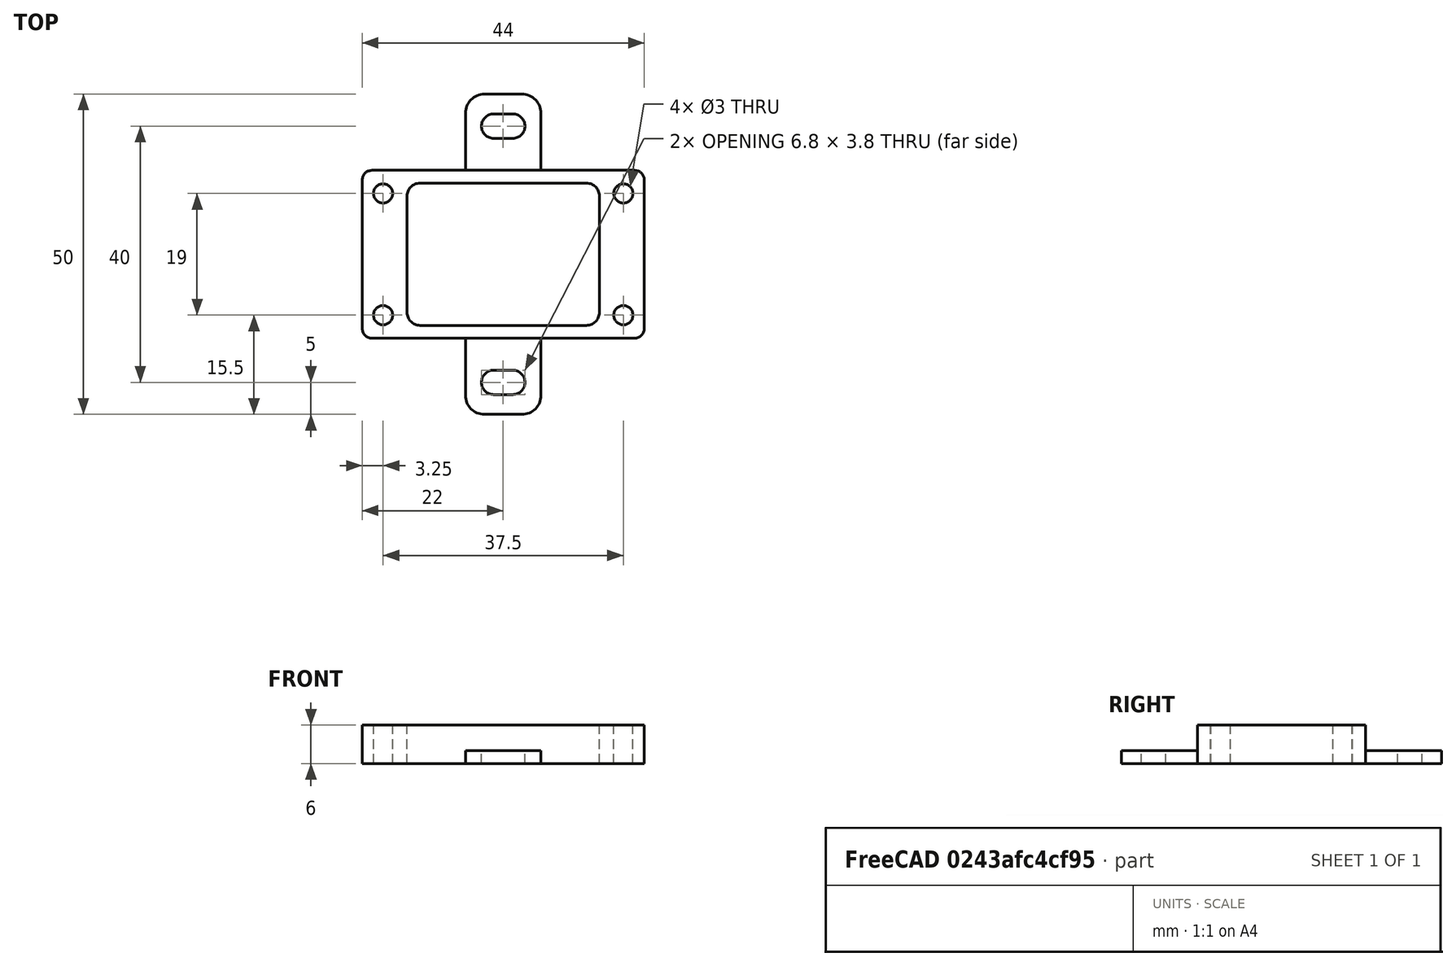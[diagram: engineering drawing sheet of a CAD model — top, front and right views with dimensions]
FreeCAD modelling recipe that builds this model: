
FCSTD DOCUMENT  (FreeCAD 0.19R23578 (Git))
Label: step_up_xl6019e1_en
License: All rights reserved
LicenseURL: http://en.wikipedia.org/wiki/All_rights_reserved
objects: Part::Box×2, Part::Fillet×2, Part::MultiFuse×2, Spreadsheet::Sheet×1, Part::Cylinder×1, Part::FeaturePython×1, Part::Feature×1, Part::Cut×1, App::Part×1
note: 10 computed .brp shape members not serialized (recipe doc carries the construction recipe); baked Part::Feature solids carry a one-line shape summary decoded from their .brp

FEATURE [Spreadsheet::Sheet] Spreadsheet  label="p"
  cells = A1=hole_x_dist; B1(hole_x_dist)=37.5; A2=hole_y_dist; B2(hole_y_dist)==pcb_y - 2 * 3.6; A3=pcb_under; B3(pcb_under)=6; A4=pcb_x; B4(pcb_x)=44; A5=pcb_y; B5(pcb_y)=26.2; A6=hole_r; B6(hole_r)=1.5; A7=under_pcb_border_x; B7(under_pcb_border_x)=7; A8=under_pcb_border_y; B8(under_pcb_border_y)=2
FEATURE [Part::Box] Box  label="bottom cube"
  AttacherType = Attacher::AttachEngine3D
  Height = 6
  Length = 44
  Width = 26.2
  expr: Width = <<p>>.pcb_y
  expr: Length = <<p>>.pcb_x
  expr: Height = <<p>>.pcb_under
FEATURE [Part::Box] Box001  label="bottom extraction cube"
  AttacherType = Attacher::AttachEngine3D
  Height = 10
  Length = 30
  Placement = pos=(7,2,0) rot=(0,0,1;0rad)
  Width = 22.2
  expr: .Placement.Base.y = Spreadsheet.under_pcb_border_y
  expr: .Placement.Base.x = Spreadsheet.under_pcb_border_x
  expr: Length = <<p>>.pcb_x - <<p>>.under_pcb_border_x * 2
  expr: Width = <<p>>.pcb_y - <<p>>.under_pcb_border_y * 2
FEATURE [Part::Cylinder] Cylinder  label="pcb hole"
  Angle = 360
  AttacherType = Attacher::AttachEngine3D
  Height = 10
  Radius = 1.5
  expr: Radius = <<p>>.hole_r
FEATURE [Part::FeaturePython] Array001  label="hole array"  # Draft array (typed FeaturePython)
  Angle = 360
  ArrayType = 0
  Axis = (0,0,1)
  Base = -> Cylinder
  Center = (0,0,0)
  Fuse = false
  IntervalAxis = (0,0,0)
  IntervalX = (37.5,0,0)
  IntervalY = (0,19,0)
  IntervalZ = (0,0,1)
  NumberPolar = 1
  NumberX = 2
  NumberY = 2
  NumberZ = 1
  Placement = pos=(3.25,3.6,0) rot=(0,0,1;0rad)
  expr: .IntervalY.y = <<p>>.hole_y_dist
  expr: .IntervalX.x = <<p>>.hole_x_dist
  expr: .Placement.Base.x = (<<p>>.pcb_x - <<p>>.hole_x_dist) / 2
  expr: .Placement.Base.y = (<<p>>.pcb_y - <<p>>.hole_y_dist) / 2
FEATURE [Part::Fillet] Fillet001  label="bottom cube fillet"
  Base = -> Box
  Edges = 4 edges r=1.5: [Edge1,Edge3,Edge5,Edge7]
FEATURE [Part::Fillet] Fillet  label="bottom extraction cube fillet"
  Base = -> Box001
  Edges = 4 edges r=2: [Edge1,Edge3,Edge5,Edge7]
FEATURE [Part::MultiFuse] Fusion  label="bottom extraction"
  Shapes = -> [Array001,Fillet]
FEATURE [Part::Feature] Cut002002  label="attach plane y dir002"
  Placement = pos=(16.1,-11.9,0) rot=(0,0,1;0rad)
  shape: bbox 11.8 x 50 x 2 mm, 20 faces (baked)
FEATURE [Part::MultiFuse] Fusion002  label="bottom fusion"
  Shapes = -> [Fillet001,Cut002002]
FEATURE [Part::Cut] Cut  label="pcb box cut"
  Base = -> Fusion002
  Tool = -> Fusion
FEATURE [App::Part] Part  label="xl6019e1_en part"
  Group = -> [Cut]
  Origin = -> Origin
